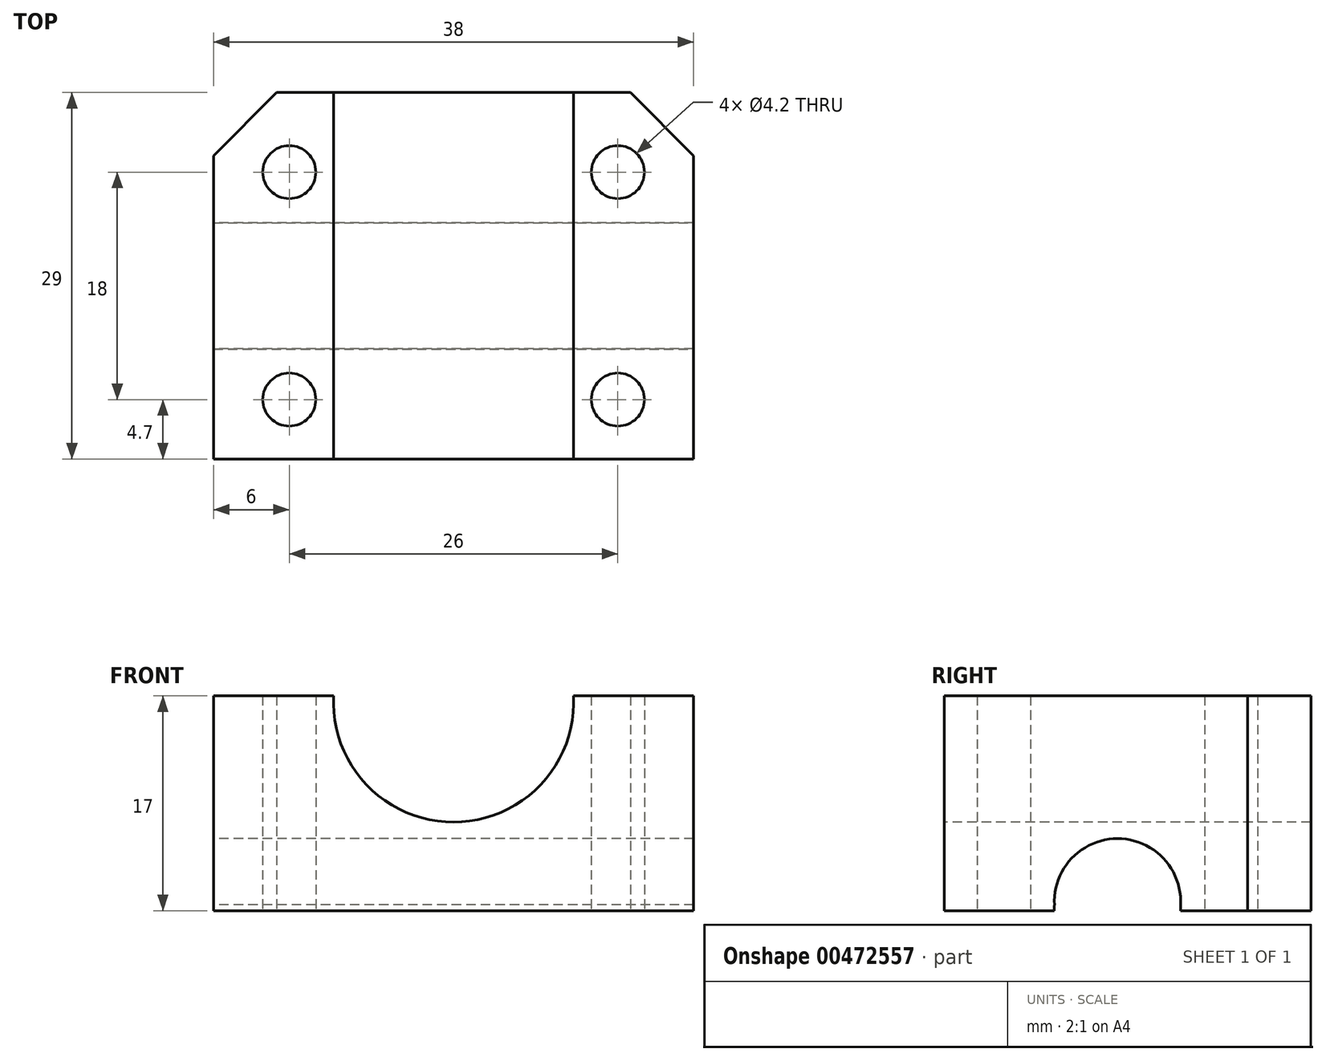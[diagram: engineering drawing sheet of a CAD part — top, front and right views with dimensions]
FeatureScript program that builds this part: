
annotation { "Feature Type Name" : "Feature", "Feature Type Description" : "" }
export const myFeature = defineFeature(function(context is Context, id is Id, definition is map)
    precondition{}
    {
        {
            var Q0;
            Q0=qCreatedBy(makeId("Top.planeOp"),FACE);
            var sketch = newSketch(context, id + "F0", { "sketchPlane" : qUnion([Q0])});
            skLineSegment(sketch, "E0.bottom", {"start": v(-14, 14.5) * mm, "end": v(14, 14.5) * mm});
            skLineSegment(sketch, "E0.top", {"start": v(-19, -14.5) * mm, "end": v(19, -14.5) * mm});
            skLineSegment(sketch, "E0.left", {"start": v(-19, 9.5) * mm, "end": v(-19, -14.5) * mm});
            skLineSegment(sketch, "E0.right", {"start": v(19, 9.5) * mm, "end": v(19, -14.5) * mm});
            skLineSegment(sketch, "E1", {"start": v(14, 14.5) * mm, "end": v(19, 9.5) * mm});
            skLineSegment(sketch, "E2.MirrorCS", {"start": v(-14, 14.5) * mm, "end": v(-19, 9.5) * mm});
            skPoint(sketch, "E3.orphan", {"position": v(19, 14.5) * mm});
            skCircle(sketch, "E4", {"center": v(-13, 8.2) * mm, "radius": 2.1 * mm});
            skCircle(sketch, "E5", {"center": v(13, 8.2) * mm, "radius": 2.1 * mm});
            skCircle(sketch, "E6", {"center": v(13, -9.8) * mm, "radius": 2.1 * mm});
            skCircle(sketch, "E7", {"center": v(-13, -9.8) * mm, "radius": 2.1 * mm});
            skSolve(sketch);
        }
        {
            var Q0;
            Q0 = qSketchRegion(id + "F0", true);
            extrude(context, id + "F1", {"entities" : qUnion([Q0]), "depth" : 19 * mm});
        }
        {
            var Q0;
            Q0=makeQuery(id+"F1.opExtrude","SWEPT_FACE",FACE,{"disambiguationData":[OSD([sQuery(id+"F0.wireOp",EDGE,"E0.top")])]});
            var sketch = newSketch(context, id + "F2", { "sketchPlane" : qUnion([Q0])});
            skLineSegment(sketch, "E8", {"start": v(-61.27, 7) * mm, "end": v(67.18, 7) * mm, "construction": true});
            skCircle(sketch, "E9", {"center": v(0, 16.5) * mm, "radius": 9.5 * mm});
            skSolve(sketch);
        }
        {
            var Q0;
            Q0 = qSketchRegion(id + "F2", true);
            extrude(context, id + "F3", {"entities" : qUnion([Q0]), "operationType" : NewBodyOperationType.REMOVE, "endBound" : BoundingType.THROUGH_ALL, "oppositeDirection" : true, "depth" : 25 * mm});
        }
        {
            var Q0;
            Q0=makeQuery(id+"F1.opExtrude","SWEPT_FACE",FACE,{"disambiguationData":[OSD([sQuery(id+"F0.wireOp",EDGE,"E0.right")])]});
            var sketch = newSketch(context, id + "F4", { "sketchPlane" : qUnion([Q0])});
            skLineSegment(sketch, "E10", {"start": v(8.2, 28.96) * mm, "end": v(8.2, -13) * mm, "construction": true});
            skLineSegment(sketch, "E11", {"start": v(-9.8, 25.88) * mm, "end": v(-9.8, -9.45) * mm, "construction": true});
            skLineSegment(sketch, "E12", {"start": v(-0.8, 23.08) * mm, "end": v(-0.8, -7.11) * mm, "construction": true});
            skCircle(sketch, "E13", {"center": v(-0.8, 0.2) * mm, "radius": 5 * mm});
            skSolve(sketch);
        }
        {
            var Q0;
            Q0 = qSketchRegion(id + "F4", true);
            extrude(context, id + "F5", {"entities" : qUnion([Q0]), "operationType" : NewBodyOperationType.REMOVE, "endBound" : BoundingType.THROUGH_ALL, "oppositeDirection" : true, "depth" : 25 * mm});
        }
        {
            var Q0;
            Q0=makeQuery(id+"F1.opExtrude","SWEPT_FACE",FACE,{"disambiguationData":[OSD([sQuery(id+"F0.wireOp",EDGE,"E0.top")])]});
            var sketch = newSketch(context, id + "F6", { "sketchPlane" : qUnion([Q0])});
            skLineSegment(sketch, "E14", {"start": v(-37.06, 17) * mm, "end": v(37.86, 17) * mm});
            skLineSegment(sketch, "E15", {"start": v(37.86, 17) * mm, "end": v(37.86, 21) * mm});
            skLineSegment(sketch, "E16", {"start": v(37.86, 21) * mm, "end": v(-37.06, 21) * mm});
            skLineSegment(sketch, "E17", {"start": v(-37.06, 21) * mm, "end": v(-37.06, 17) * mm});
            skSolve(sketch);
        }
        {
            var Q0;
            Q0 = qSketchRegion(id + "F6", true);
            extrude(context, id + "F7", {"entities" : qUnion([Q0]), "operationType" : NewBodyOperationType.REMOVE, "endBound" : BoundingType.THROUGH_ALL, "oppositeDirection" : true, "depth" : 25 * mm});
        }
        {
            var Q0;
            Q0=makeQuery(id+"F1.opExtrude","SWEPT_FACE",FACE,{"disambiguationData":[OSD([sQuery(id+"F0.wireOp",EDGE,"E0.left")])]});
            var sketch = newSketch(context, id + "F8", { "sketchPlane" : qUnion([Q0])});
            skLineSegment(sketch, "E18", {"start": v(0.8, 5.2) * mm, "end": v(0.8, -2.58) * mm, "construction": true});
            skLineSegment(sketch, "E19", {"start": v(0.8, 0.2) * mm, "end": v(5.4, 0.2) * mm, "construction": true});
            skCircle(sketch, "E20", {"center": v(0.8, 0.7) * mm, "radius": 5 * mm});
            skSolve(sketch);
        }
        {
            var Q0;
            Q0 = qSketchRegion(id + "F8", true);
            extrude(context, id + "F9", {"entities" : qUnion([Q0]), "operationType" : NewBodyOperationType.REMOVE, "endBound" : BoundingType.THROUGH_ALL, "oppositeDirection" : true, "depth" : 25 * mm});
        }
    });
